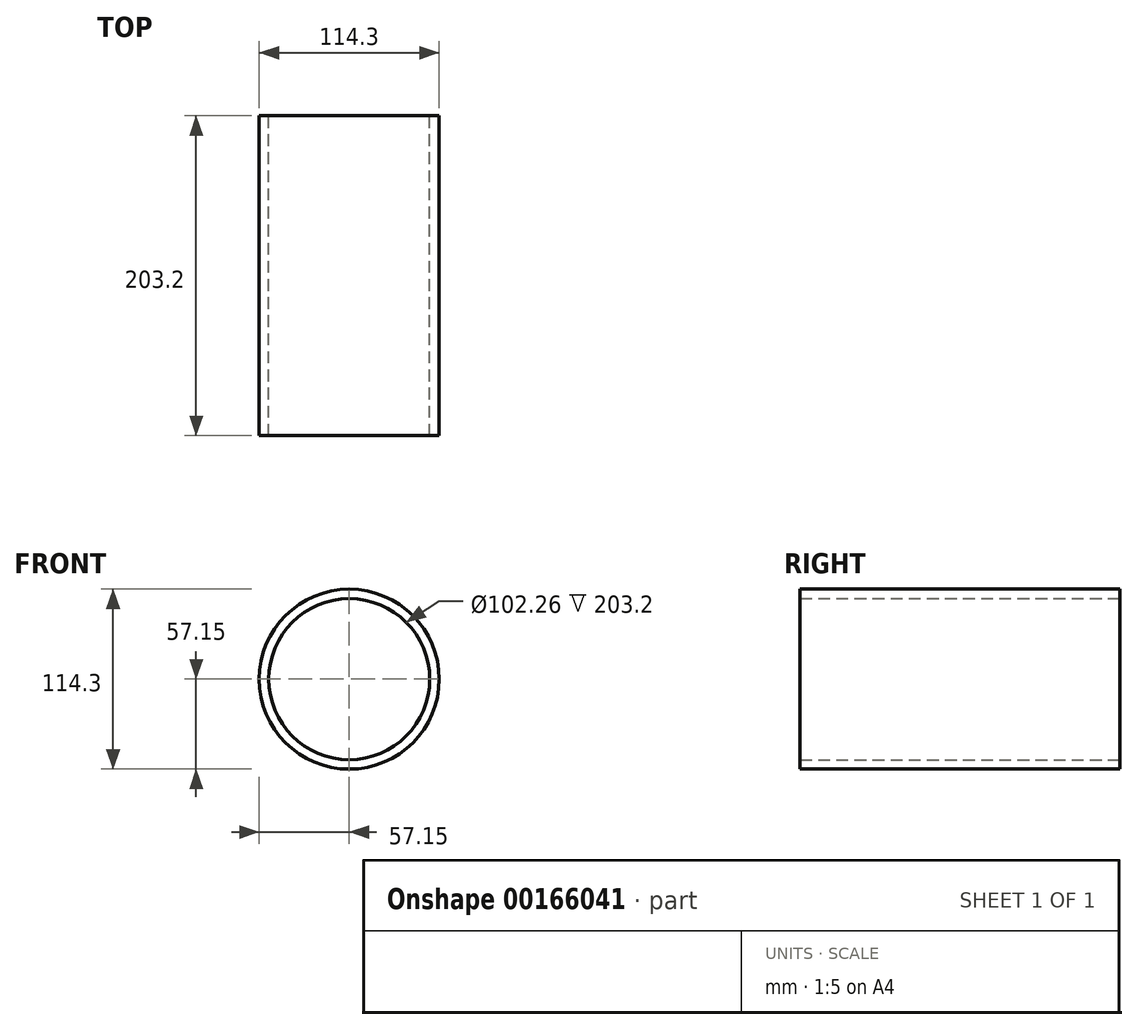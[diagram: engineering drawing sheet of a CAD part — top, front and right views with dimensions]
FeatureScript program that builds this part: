
annotation { "Feature Type Name" : "Feature", "Feature Type Description" : "" }
export const myFeature = defineFeature(function(context is Context, id is Id, definition is map)
    precondition{}
    {
        {
            var Q0;
            Q0=qCreatedBy(makeId("Front.planeOp"),FACE);
            var sketch = newSketch(context, id + "F0", { "sketchPlane" : qUnion([Q0])});
            skCircle(sketch, "E0", {"center": v(0, 0) * mm, "radius": 51.13 * mm});
            skCircle(sketch, "E1", {"center": v(0, 0) * mm, "radius": 57.15 * mm});
            skSolve(sketch);
        }
        {
            var Q0;
            Q0=makeQuery(id+"F0.imprint","IMPRINT",FACE,{"disambiguationData":[TD([[makeQuery(id+"F0.imprint","IMPRINT",EDGE,{"derivedFrom":sQuery(id+"F0.wireOp",EDGE,"E0")}),-1.0]])]});
            extrude(context, id + "F1", {"entities" : qUnion([Q0]), "endBound" : BoundingType.SYMMETRIC, "depth" : 203.2 * mm});
        }
    });
